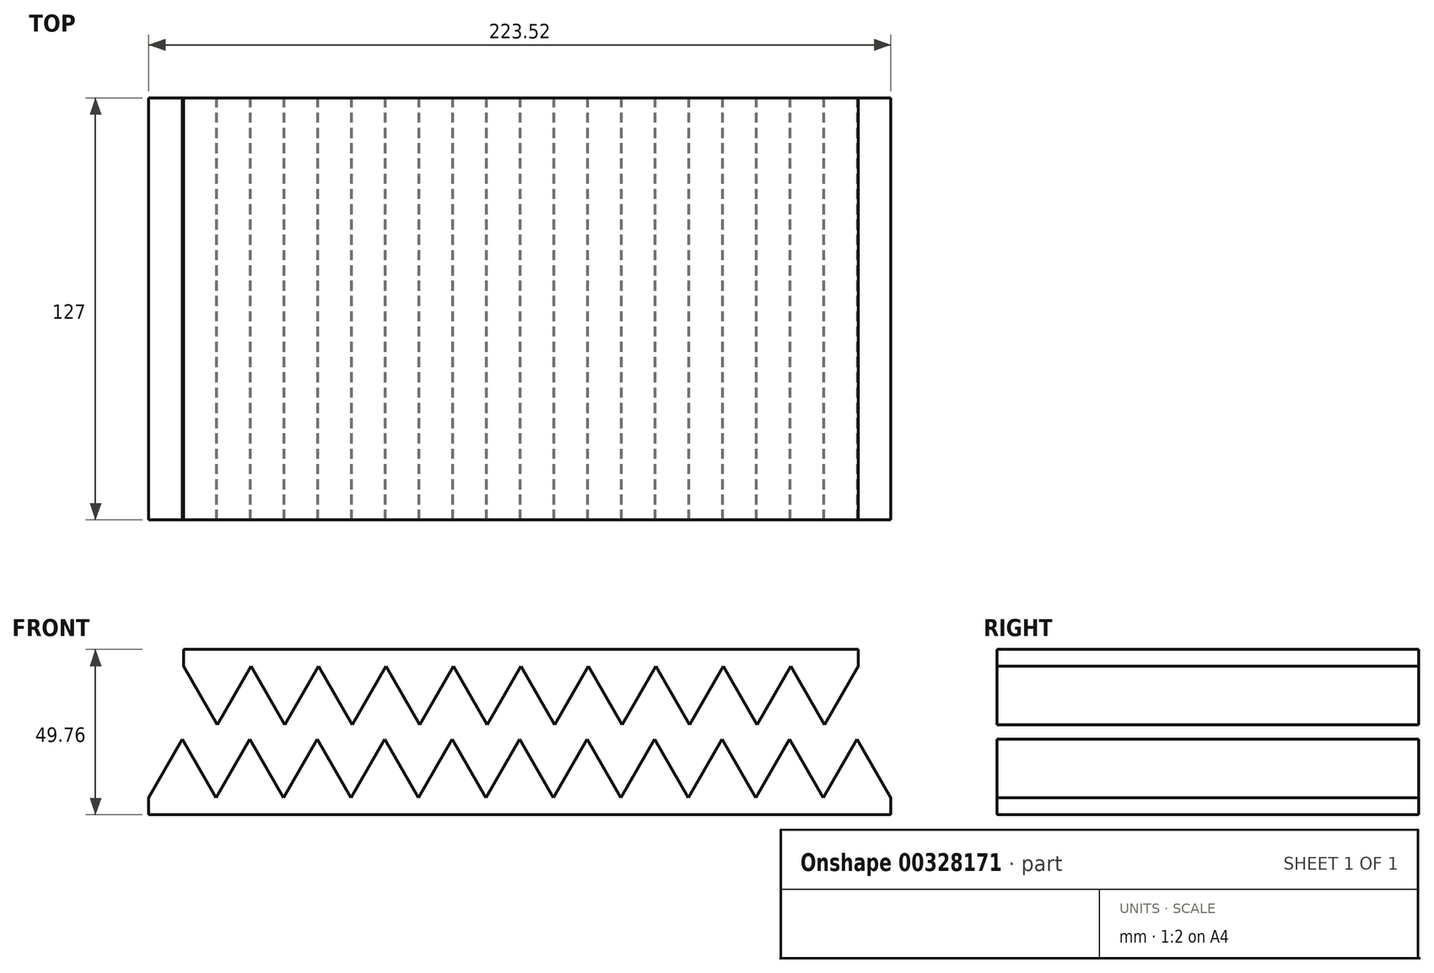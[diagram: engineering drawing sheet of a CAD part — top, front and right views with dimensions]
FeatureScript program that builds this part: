
annotation { "Feature Type Name" : "Feature", "Feature Type Description" : "" }
export const myFeature = defineFeature(function(context is Context, id is Id, definition is map)
    precondition{}
    {
        {
            var Q0;
            Q0=qCreatedBy(makeId("Front.planeOp"),FACE);
            var sketch = newSketch(context, id + "F0", { "sketchPlane" : qUnion([Q0])});
            skLineSegment(sketch, "E0.bottom", {"start": v(-154.18, 27.08) * mm, "end": v(49.02, 27.08) * mm});
            skLineSegment(sketch, "E0.left", {"start": v(-154.18, 27.08) * mm, "end": v(-154.18, 22) * mm});
            skLineSegment(sketch, "E0.right", {"start": v(49.02, 27.08) * mm, "end": v(49.02, 22) * mm});
            skPoint(sketch, "E1.start.orphan", {"position": v(-133.86, 22) * mm});
            skPoint(sketch, "E2.end.orphan", {"position": v(-113.54, 22) * mm});
            skPoint(sketch, "E2.start.orphan", {"position": v(-68.49, 0) * mm});
            skLineSegment(sketch, "E3", {"start": v(-154.18, 22) * mm, "end": v(-144.02, 4.4) * mm});
            skLineSegment(sketch, "E4", {"start": v(-144.02, 4.4) * mm, "end": v(-133.86, 22) * mm});
            skLineSegment(sketch, "E5", {"start": v(-133.86, 22) * mm, "end": v(-123.7, 4.4) * mm});
            skLineSegment(sketch, "E6", {"start": v(-123.7, 4.4) * mm, "end": v(-113.54, 22) * mm});
            skLineSegment(sketch, "E7", {"start": v(-113.54, 22) * mm, "end": v(-103.38, 4.4) * mm});
            skLineSegment(sketch, "E8", {"start": v(-103.38, 4.4) * mm, "end": v(-93.22, 22) * mm});
            skLineSegment(sketch, "E9", {"start": v(-93.22, 22) * mm, "end": v(-83.06, 4.4) * mm});
            skLineSegment(sketch, "E10", {"start": v(-83.06, 4.4) * mm, "end": v(-72.9, 22) * mm});
            skLineSegment(sketch, "E11", {"start": v(-72.9, 22) * mm, "end": v(-62.74, 4.4) * mm});
            skLineSegment(sketch, "E12", {"start": v(-62.74, 4.4) * mm, "end": v(-52.58, 22) * mm});
            skLineSegment(sketch, "E13", {"start": v(-52.58, 22) * mm, "end": v(-42.42, 4.4) * mm});
            skLineSegment(sketch, "E14", {"start": v(-42.42, 4.4) * mm, "end": v(-32.26, 22) * mm});
            skLineSegment(sketch, "E15", {"start": v(-32.26, 22) * mm, "end": v(-22.1, 4.4) * mm});
            skLineSegment(sketch, "E16", {"start": v(-22.1, 4.4) * mm, "end": v(-11.94, 22) * mm});
            skLineSegment(sketch, "E17", {"start": v(-11.94, 22) * mm, "end": v(-1.78, 4.4) * mm});
            skLineSegment(sketch, "E18", {"start": v(-1.78, 4.4) * mm, "end": v(8.38, 22) * mm});
            skLineSegment(sketch, "E19", {"start": v(8.38, 22) * mm, "end": v(18.54, 4.4) * mm});
            skLineSegment(sketch, "E20", {"start": v(18.54, 4.4) * mm, "end": v(28.7, 22) * mm});
            skLineSegment(sketch, "E21", {"start": v(28.7, 22) * mm, "end": v(38.86, 4.4) * mm});
            skLineSegment(sketch, "E22", {"start": v(38.86, 4.4) * mm, "end": v(49.02, 22) * mm});
            skLineSegment(sketch, "E23", {"start": v(-88.49, 61.41) * mm, "end": v(161.51, 61.41) * mm});
            skLineSegment(sketch, "E24", {"start": v(-164.65, -17.6) * mm, "end": v(-154.5, 0) * mm});
            skLineSegment(sketch, "E25", {"start": v(-154.5, 0) * mm, "end": v(-144.33, -17.6) * mm});
            skLineSegment(sketch, "E26", {"start": v(-144.33, -17.6) * mm, "end": v(-134.17, 0) * mm});
            skLineSegment(sketch, "E27", {"start": v(-134.17, 0) * mm, "end": v(-124.01, -17.6) * mm});
            skLineSegment(sketch, "E28", {"start": v(-124.01, -17.6) * mm, "end": v(-113.85, 0) * mm});
            skLineSegment(sketch, "E29", {"start": v(-113.85, 0) * mm, "end": v(-103.7, -17.6) * mm});
            skLineSegment(sketch, "E30", {"start": v(-103.7, -17.6) * mm, "end": v(-93.53, 0) * mm});
            skLineSegment(sketch, "E31", {"start": v(-93.53, 0) * mm, "end": v(-83.37, -17.6) * mm});
            skLineSegment(sketch, "E32", {"start": v(-83.37, -17.6) * mm, "end": v(-73.21, 0) * mm});
            skLineSegment(sketch, "E33", {"start": v(-73.21, 0) * mm, "end": v(-63.05, -17.6) * mm});
            skLineSegment(sketch, "E34", {"start": v(-63.05, -17.6) * mm, "end": v(-52.9, 0) * mm});
            skLineSegment(sketch, "E35", {"start": v(-52.9, 0) * mm, "end": v(-42.73, -17.6) * mm});
            skLineSegment(sketch, "E36", {"start": v(-42.73, -17.6) * mm, "end": v(-32.57, 0) * mm});
            skLineSegment(sketch, "E37", {"start": v(-32.57, 0) * mm, "end": v(-22.41, -17.6) * mm});
            skLineSegment(sketch, "E38", {"start": v(-22.41, -17.6) * mm, "end": v(-12.25, 0) * mm});
            skLineSegment(sketch, "E39", {"start": v(-12.25, 0) * mm, "end": v(-2.1, -17.6) * mm});
            skLineSegment(sketch, "E40", {"start": v(-2.1, -17.6) * mm, "end": v(8.07, 0) * mm});
            skLineSegment(sketch, "E41", {"start": v(8.07, 0) * mm, "end": v(18.23, -17.6) * mm});
            skLineSegment(sketch, "E42", {"start": v(18.23, -17.6) * mm, "end": v(28.39, 0) * mm});
            skLineSegment(sketch, "E43", {"start": v(28.39, 0) * mm, "end": v(38.55, -17.6) * mm});
            skLineSegment(sketch, "E44", {"start": v(38.55, -17.6) * mm, "end": v(48.7, 0) * mm});
            skLineSegment(sketch, "E45", {"start": v(48.7, 0) * mm, "end": v(58.87, -17.6) * mm});
            skLineSegment(sketch, "E46.top", {"start": v(-164.65, -22.68) * mm, "end": v(58.87, -22.68) * mm});
            skLineSegment(sketch, "E46.left", {"start": v(-164.65, -17.6) * mm, "end": v(-164.65, -22.68) * mm});
            skLineSegment(sketch, "E46.right", {"start": v(58.87, -17.6) * mm, "end": v(58.87, -22.68) * mm});
            skLineSegment(sketch, "E47", {"start": v(-164.65, -17.6) * mm, "end": v(-164.65, -60.63) * mm});
            skLineSegment(sketch, "E48", {"start": v(-164.65, -60.63) * mm, "end": v(-154.5, -43.03) * mm});
            skLineSegment(sketch, "E49", {"start": v(-154.5, -43.03) * mm, "end": v(-164.65, -43.03) * mm});
            skLineSegment(sketch, "E50", {"start": v(-164.65, -60.63) * mm, "end": v(-167.2, -60.63) * mm});
            skLineSegment(sketch, "E51", {"start": v(-167.2, -60.63) * mm, "end": v(-167.2, -65.71) * mm});
            skLineSegment(sketch, "E52", {"start": v(-167.2, -65.71) * mm, "end": v(-167.2, -40.26) * mm});
            skPoint(sketch, "E52.endSnap0", {"position": v(-167.2, -63.17) * mm});
            skLineSegment(sketch, "E53", {"start": v(-164.65, -43.03) * mm, "end": v(-167.2, -43.03) * mm});
            skLineSegment(sketch, "E54", {"start": v(-164.65, -17.6) * mm, "end": v(-144.33, -17.6) * mm});
            skLineSegment(sketch, "E55", {"start": v(-154.5, 0) * mm, "end": v(-154.5, -17.6) * mm});
            skLineSegment(sketch, "E56", {"start": v(-164.65, -65.71) * mm, "end": v(-164.65, -60.63) * mm});
            skLineSegment(sketch, "E57", {"start": v(-167.2, -65.71) * mm, "end": v(-164.65, -65.71) * mm});
            skLineSegment(sketch, "E58", {"start": v(-164.65, -65.71) * mm, "end": v(-164.65, -77.62) * mm});
            skLineSegment(sketch, "E59", {"start": v(-164.65, -77.62) * mm, "end": v(58.87, -77.62) * mm});
            skSolve(sketch);
        }
        {
            var Q0;
            Q0=makeQuery(id+"F0.imprint","IMPRINT",FACE,{"disambiguationData":[TD([[makeQuery(id+"F0.imprint","IMPRINT",EDGE,{"derivedFrom":sQuery(id+"F0.wireOp",EDGE,"E0.bottom")}),-1.0]])]});
            var Q1;
            Q1=makeQuery(id+"F0.imprint","IMPRINT",FACE,{"disambiguationData":[TD([[makeQuery(id+"F0.imprint","IMPRINT",EDGE,{"derivedFrom":sQuery(id+"F0.wireOp",EDGE,"E24")}),-1.0]])]});
            var Q2;
            {var subQ0=sQuery(id+"F0.wireOp",EDGE,"E25");Q2=makeQuery(id+"F0.imprint","IMPRINT",FACE,{"disambiguationData":[TD([[makeQuery(id+"F0.imprint","IMPRINT",EDGE,{"derivedFrom":subQ0}),-1.0]])]});}
            var Q3;
            {var subQ1=sQuery(id+"F0.wireOp",EDGE,"E26");Q3=makeQuery(id+"F0.imprint","IMPRINT",FACE,{"disambiguationData":[TD([[makeQuery(id+"F0.imprint","IMPRINT",EDGE,{"derivedFrom":subQ1}),-1.0]])]});}
            extrude(context, id + "F1", {"entities" : qUnion([Q0, Q1, Q2, Q3]), "depth" : 127 * mm, "offsetDistance" : 25.4 * mm});
        }
    });
